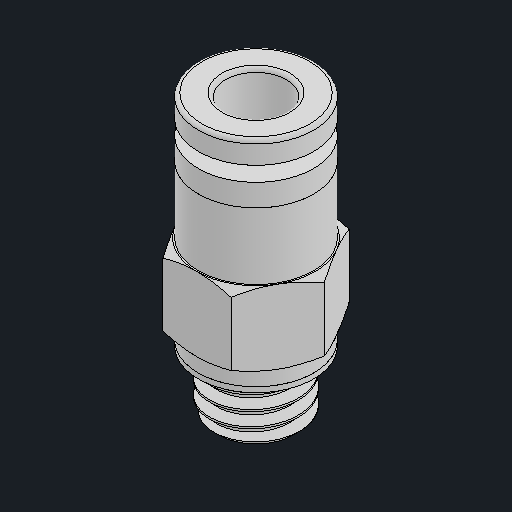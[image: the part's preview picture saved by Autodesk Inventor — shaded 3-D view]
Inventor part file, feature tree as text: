
AUTODESK INVENTOR PART (.ipt)
format: ipt  version: 2024.2 (Build 282272000, 272)  size: 291,328 bytes
history: native  units: mm
features: other x4, fillet x1, chamfer x1
ambient origin geometry x8: Origin, YZ Plane, XZ Plane, XY Plane, X Axis, Y Axis, Z Axis, Center Point
bodies: Body1 (feature_tree), Body2 (feature_tree), Body3 (feature_tree)
feature tree (6):
  other  "솔리드1"
  other  "솔리드2"
  other  "솔리드3"
  fillet  "Fillet1"  [1 undecoded]
  other  "Boss-Extrude6"
  chamfer  "Chamfer2"  [1 undecoded]
note: 2 required parameter values undecoded (feature->parameter linkage not recoverable at this tier; creation-order binding heuristic only, values carry confidence <= 0.55)
